# Revit family: Camera-Security-Panasonic-Super_Dynamic-H265_Network-BoxAI_Engine-WV-S1136SeriesX
name_source: partatom
category: Security Devices
units: mm (PartAtom-declared; Revit-internal decimal feet)

## family parameters
Always vertical = No
Cut with Voids When Loaded = No
Maintain Annotation Orientation = No
OmniClass Number = 23.85.10.14.11
OmniClass Title = Cameras
Part Type = Normal
Room Calculation Point = No
Round Connector Dimension = Use Diameter
Shared = No
Work Plane-Based = Yes

## types (1)
- WV-S1136
    Alarm Input Or Output Specification = ALARM IN 1 (Black & white input, Auto time adjustment input) (x1), ALARM IN 2 (ALARM OUT) (x1),  LARM IN 3 (AUX OUT) (x1)
    Angle Of View = Lens Dependent
    Audio In = ø3.5 mm stereo mini jack
    Audio Out = ø3.5 mm stereo mini jack (monaural output)
    Auto Back Focus = Yes
    Body Radius = 1.398 "
    Communication Ports = 10Base-T / 100Base-TX, RJ45 connector
    Date Last Modified = 2021/04/09
    Day Or Night = Yes
    Default Elevation = 48 "
    Depth = 5.748 "
    Description = Security Camera, Network, Super Dynamic, AI Engine, Full HD, H.265 BOX Camera, WV-S1136
    Equipment Abbreviation = SC
    Family Version = 1.0.0
    Has POE = Yes
    Height = 2.244 "
    IP Or Analog = IP
    Indoor Or Outdoor = Indoor
    Manufacturer = Panasonic
    Minimum Illumination = 0.006 lx
    Model = WV-S1136
    Model Disclaimer = Contact Panasonic for more information
    Mounting Positions = Mount Dependent
    Operational Humidity = 10 to 90 % (no condensation)
    Operational Temperature = -10 °C to +50 °C (14 °F to 122 °F)
    Part Description = Security Camera, Network, Super Dynamic, AI Engine, Full HD, H.265 BOX Camera, WV-S1136
    Part Number = WV-S1136
    Product Documentation Link = https://bizpartner.panasonic.net
    Product Material = Paint - Panasonic - i-PRO White
    Product Page URL = https://security.panasonic.com
    Provide Feedback = https://www.surveymonkey.com
    Regulatory Compliance = UL (UL62368-1), c-UL (CSA C22.2 No.62368-1), CE, IEC62368-1, FCC (Part15 ClassA), ICES-003 ClassA, EN55032 ClassB, EN55035
    Storage Temperature = -10 °C to +50 °C (14 °F to 122 °F)
    URL = http://security.panasonic.com
    Vandal Resistant = No
    Weight = 0.82 lb
    Wide Dynamic Range = Yes
    Width = 2.953 "

## geometry (parser evidence)
native form markers: Blend x2, Sweep x3
no freeform markers — native parametric forms only
